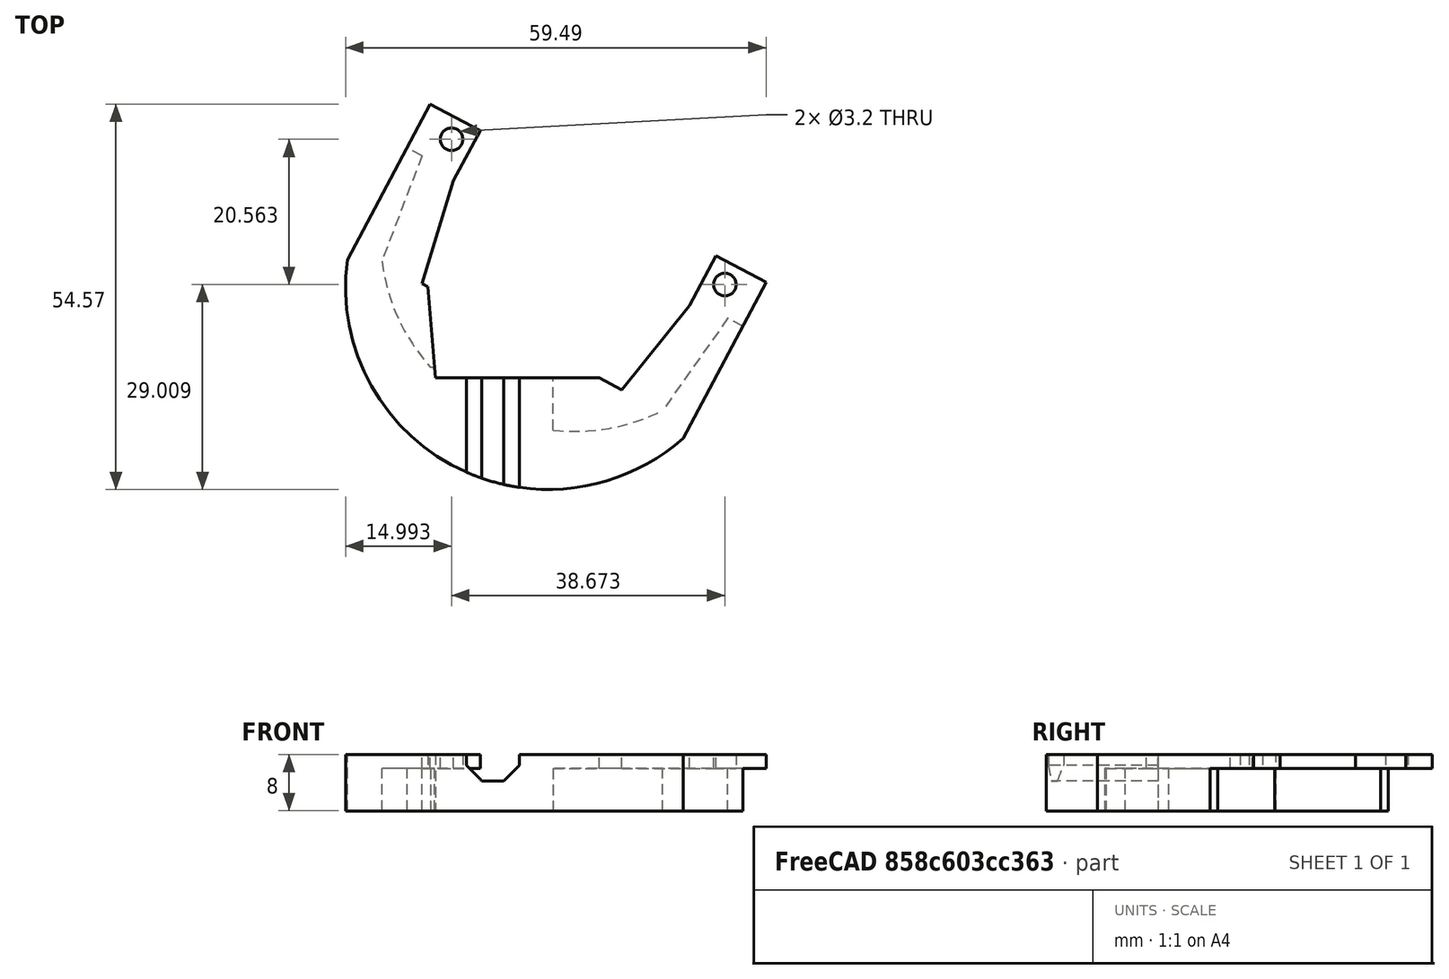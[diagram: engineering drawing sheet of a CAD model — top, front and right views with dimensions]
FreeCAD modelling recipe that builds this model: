
FCSTD DOCUMENT  (FreeCAD 0.19R)
Label: UmbilicalStrainReleif
License: All rights reserved
LicenseURL: http://en.wikipedia.org/wiki/All_rights_reserved
objects: Sketcher::SketchObject×5, PartDesign::Pocket×3, PartDesign::Pad×2, PartDesign::Body×1, Mesh::Feature×1
note: 16 computed .brp shape members not serialized (recipe doc carries the construction recipe); baked Part::Feature solids carry a one-line shape summary decoded from their .brp

FEATURE [Sketcher::SketchObject] Sketch
  FullyConstrained = false
  MapMode = 5
  Placement = pos=(0,4.01e-14,34.3878) rot=(0,0,1;3.14159rad)
  sketch-geometry (14):
    g0: Circle CenterX=-19.3366 CenterY=10.2814 CenterZ=0 NormalX=0 NormalY=0 NormalZ=1 AngleXU=0 Radius=1.6
    g1: Circle CenterX=19.3366 CenterY=-10.2814 CenterZ=0 NormalX=0 NormalY=0 NormalZ=1 AngleXU=0 Radius=1.6
    g2: LineSegment StartX=-19.3366 StartY=10.2814 StartZ=0 EndX=19.3366 EndY=-10.2814 EndZ=0
    g3: LineSegment StartX=-25.1597 StartY=9.97994 StartZ=0 EndX=-13.4229 EndY=32.0536 EndZ=0
    g4: LineSegment StartX=34.0797 StartY=6.79606 StartZ=0 EndX=22.3429 EndY=-15.2776 EndZ=0
    g5: LineSegment StartX=22.3429 StartY=-15.2776 StartZ=0 EndX=15.2793 EndY=-11.5219 EndZ=0
    g6: LineSegment StartX=23.5166 StartY=10.1474 StartZ=0 EndX=-4.73773 EndY=25.1705 EndZ=0
    g7: LineSegment StartX=-18.0961 StartY=6.22417 StartZ=0 EndX=-25.1597 EndY=9.97994 EndZ=0
    g8: LineSegment StartX=15.2793 StartY=-11.5219 StartZ=0 EndX=19.0351 EndY=-4.45827 EndZ=0
    g9: LineSegment StartX=19.0351 StartY=-4.45827 StartZ=0 EndX=23.5166 EndY=10.1474 EndZ=0
    g10: LineSegment StartX=-18.0961 StartY=6.22417 StartZ=0 EndX=-14.3404 EndY=13.2878 EndZ=0
    g11: LineSegment StartX=-14.3404 StartY=13.2878 StartZ=0 EndX=-4.73773 EndY=25.1705 EndZ=0
    g12: LineSegment StartX=0 StartY=0 StartZ=0 EndX=21.8903 EndY=41.1697 EndZ=0
    g13: ArcOfCircle CenterX=5.63366 CenterY=10.5954 CenterZ=0 NormalX=0 NormalY=0 NormalZ=1 AngleXU=0 Radius=28.6986 StartAngle=6.15041 EndAngle=8.58017
  constraints (38):
    c: Distance(g1,g0) = 43.8
    c: Symmetric(g1,g0,g-1)
    c: Coincident(g2,g0)
    c: Coincident(g2,g1)
    c: Angle(g2) = -0.488692
    c: Coincident(g4,g5)
    c: Coincident(g7,g3)
    c: Diameter(g1) = 3.2
    c: Equal(g1,g0)
    c: Distance(g1,g5) = 3
    c: Distance(g0,g7) = 3
    c: Parallel(g5,g2)
    c: Parallel(g7,g2)
    c: Distance(g5) = 8
    c: Distance(g7) = 8
    c: Parallel(g6,g2)
    c: Distance(g6,g2) = 20
    c: Coincident(g5,g8)
    c: Coincident(g8,g9)
    c: Coincident(g9,g6)
    c: Coincident(g7,g10)
    c: Coincident(g10,g11)
    c: Coincident(g11,g6)
    c: Coincident(g12,g-1)
    c: Symmetric(g6,g6,g12)
    c: Distance(g6) = 32
    c: Perpendicular(g2,g8)
    c: Perpendicular(g2,g10)
    c: Distance(g1,g8) = 3
    c: Distance(g0,g10) = 3
    c: Symmetric(g4,g3,g12)
    c: Distance(g10) = 8
    c: Distance(g8) = 8
    c: Perpendicular(g2,g4)
    c: Distance(g4) = 25
    c: Coincident(g13,g3)
    c: Coincident(g4,g13)
    c: Distance(g-1,g13) = 12
FEATURE [PartDesign::Pad] Pad
  Direction = (1,1,1)
  Length = 8
  Length2 = 100
  Placement = pos=(0,4.01e-14,34.3878) rot=(0,0,1;3.14159rad)
  Profile = -> Sketch
  Type = 0
FEATURE [Sketcher::SketchObject] Sketch001
  FullyConstrained = true
  MapMode = 5
  Placement = pos=(0,4.01e-14,34.3878) rot=(0,1,0;3.14159rad)
  Support = -> [Pad]
  sketch-geometry (4):
    g0: LineSegment StartX=5 StartY=-22 StartZ=0 EndX=23 EndY=-22 EndZ=0
    g1: LineSegment StartX=23 StartY=-22 StartZ=0 EndX=23 EndY=-32 EndZ=0
    g2: LineSegment StartX=23 StartY=-32 StartZ=0 EndX=5 EndY=-32 EndZ=0
    g3: LineSegment StartX=5 StartY=-32 StartZ=0 EndX=5 EndY=-22 EndZ=0
  constraints (12):
    c: Coincident(g0,g1)
    c: Coincident(g1,g2)
    c: Coincident(g2,g3)
    c: Coincident(g3,g0)
    c: Horizontal(g0)
    c: Horizontal(g2)
    c: Vertical(g1)
    c: Vertical(g3)
    c: Distance(g0) = 18
    c: Distance(g1) = 10
    c: DistanceX(g0) = 5
    c: DistanceY(g0) = -22
FEATURE [Sketcher::SketchObject] Sketch004
  ExternalGeometry = -> [Pad]
  FullyConstrained = true
  MapMode = 5
  Placement = pos=(0,4.01e-14,34.3878) rot=(0,1,0;3.14159rad)
  sketch-geometry (10):
    g0: ArcOfCircle CenterX=1.87789 CenterY=-3.53179 CenterZ=0 NormalX=0 NormalY=0 NormalZ=1 AngleXU=0 Radius=27.5363 StartAngle=4.24472 EndAngle=6.15745
    g1: LineSegment StartX=23.5101 StartY=7.97026 StartZ=0 EndX=29.1968 EndY=-6.98504 EndZ=0
    g2: LineSegment StartX=-19.7543 StartY=-15.0338 StartZ=0 EndX=-10.5358 EndY=-28.1113 EndZ=0
    g3: LineSegment StartX=23.5101 StartY=7.97026 StartZ=0 EndX=33.7655 EndY=13.4232 EndZ=0
    g4: LineSegment StartX=33.7655 StartY=13.4232 StartZ=0 EndX=24.3761 EndY=31.0821 EndZ=0
    g5: LineSegment StartX=24.3761 StartY=31.0821 StartZ=0 EndX=-39.3992 EndY=-2.8278 EndZ=0
    g6: LineSegment StartX=-39.3992 StartY=-2.8278 StartZ=0 EndX=-30.0098 EndY=-20.4868 EndZ=0
    g7: LineSegment StartX=-30.0098 StartY=-20.4868 StartZ=0 EndX=-19.7543 EndY=-15.0338 EndZ=0
    g8: LineSegment StartX=0 StartY=0 StartZ=0 EndX=22.3656 EndY=-42.0636 EndZ=0
    g9: LineSegment StartX=-19.3366 StartY=-10.2814 StartZ=0 EndX=19.3366 EndY=10.2814 EndZ=0
  constraints (27):
    c: Coincident(g1,g0)
    c: Coincident(g2,g0)
    c: Coincident(g1,g3)
    c: Coincident(g3,g4)
    c: Coincident(g4,g5)
    c: Coincident(g5,g6)
    c: Coincident(g6,g7)
    c: Coincident(g7,g2)
    c: Symmetric(g2,g1,g0)
    c: Coincident(g8,g-1)
    c: Coincident(g9,g-3)
    c: Coincident(g9,g-4)
    c: Perpendicular(g9,g8)
    c: Parallel(g7,g9)
    c: Symmetric(g0,g0,g8)
    c: Distance(g0,g0) = 45
    c: Distance(g2) = 16
    c: Symmetric(g1,g2,g8)
    c: Distance(g1,g2) = 49
    c: Distance(g1,g9) = 4
    c: Symmetric(g3,g6,g8)
    c: Parallel(g5,g9)
    c: Perpendicular(g4,g3)
    c: Perpendicular(g6,g7)
    c: Distance(g6) = 20
    c: Distance(g5) = 72.23
    c: Distance(g8) = 47.64
FEATURE [PartDesign::Pocket] Pocket
  BaseFeature = -> Pad
  Length = 6
  Length2 = 100
  Placement = pos=(0,4.01e-14,34.3878) rot=(0,0,1;3.14159rad)
  Profile = -> Sketch004
  Type = 0
FEATURE [PartDesign::Pad] Pad001
  BaseFeature = -> Pocket
  Direction = (1,1,1)
  Length = 8
  Length2 = 100
  Placement = pos=(0,4.01e-14,34.3878) rot=(0,0,1;3.14159rad)
  Profile = -> Sketch001
  Reversed = true
  Type = 0
FEATURE [Sketcher::SketchObject] Sketch006
  FullyConstrained = true
  MapMode = 5
  Placement = pos=(2.7e-15,-22,34.3878) rot=(0,0.707107,0.707107;3.14159rad)
  Support = -> [Pad001]
  sketch-geometry (7):
    g0: Circle CenterX=13.5 CenterY=8 CenterZ=0 NormalX=0 NormalY=0 NormalZ=1 AngleXU=0 Radius=3.75
    g1: LineSegment StartX=11.9467 StartY=4.25 StartZ=0 EndX=15.0533 EndY=4.25 EndZ=0
    g2: LineSegment StartX=15.0533 StartY=4.25 StartZ=0 EndX=17.25 EndY=6.4467 EndZ=0
    g3: LineSegment StartX=17.25 StartY=6.4467 StartZ=0 EndX=17.25 EndY=9.4467 EndZ=0
    g4: LineSegment StartX=17.25 StartY=9.4467 StartZ=0 EndX=9.75 EndY=9.4467 EndZ=0
    g5: LineSegment StartX=9.75 StartY=9.4467 StartZ=0 EndX=9.75 EndY=6.4467 EndZ=0
    g6: LineSegment StartX=9.75 StartY=6.4467 StartZ=0 EndX=11.9467 EndY=4.25 EndZ=0
  constraints (21):
    c: Diameter(g0) = 7.5
    c: DistanceY(g0) = 8
    c: DistanceX(g0) = 13.5
    c: Horizontal(g1)
    c: Tangent(g1,g0)
    c: Coincident(g1,g2)
    c: Coincident(g2,g3)
    c: Vertical(g3)
    c: Tangent(g3,g0)
    c: Coincident(g3,g4)
    c: Coincident(g4,g5)
    c: Vertical(g5)
    c: Coincident(g5,g6)
    c: Coincident(g6,g1)
    c: Horizontal(g4)
    c: Equal(g5,g3)
    c: Equal(g2,g6)
    c: Equal(g1,g2)
    c: Angle(g2) = 0.785398
    c: Distance(g4) = 7.5
    c: Distance(g3) = 3
FEATURE [PartDesign::Pocket] Pocket001
  BaseFeature = -> Pad001
  Length = 34
  Length2 = 12
  Placement = pos=(0,4.01e-14,34.3878) rot=(0,0,1;3.14159rad)
  Profile = -> Sketch006
  Type = 4
FEATURE [Sketcher::SketchObject] Sketch007
  FullyConstrained = false
  MapMode = 5
  Placement = pos=(1e-16,4.95e-14,42.3878) rot=(0,0,1;3.14159rad)
  Support = -> [Pocket001]
  sketch-geometry (3):
    g0: LineSegment StartX=-3.52213 StartY=23.4904 StartZ=0 EndX=21.5979 EndY=23.4904 EndZ=0
    g1: LineSegment StartX=21.5979 StartY=23.4904 StartZ=0 EndX=22.7514 EndY=9.52057 EndZ=0
    g2: LineSegment StartX=22.7514 StartY=9.52057 StartZ=0 EndX=-3.52213 EndY=23.4904 EndZ=0
  constraints (4):
    c: Horizontal(g0)
    c: Coincident(g0,g1)
    c: Coincident(g1,g2)
    c: Coincident(g2,g0)
FEATURE [PartDesign::Pocket] Pocket002
  BaseFeature = -> Pocket001
  Length = 5
  Length2 = 100
  Placement = pos=(0,4.01e-14,34.3878) rot=(0,0,1;3.14159rad)
  Profile = -> Sketch007
  Type = 1
FEATURE [PartDesign::Body] Body
  Group = -> [Sketch,Pad,Sketch001,Sketch004,Pocket,Pad001,Sketch006,Pocket001,Sketch007,Pocket002]
  Origin = -> Origin
  Tip = -> Pocket002
FEATURE [Mesh::Feature] Mesh  label="Pocket002 (Meshed)"
